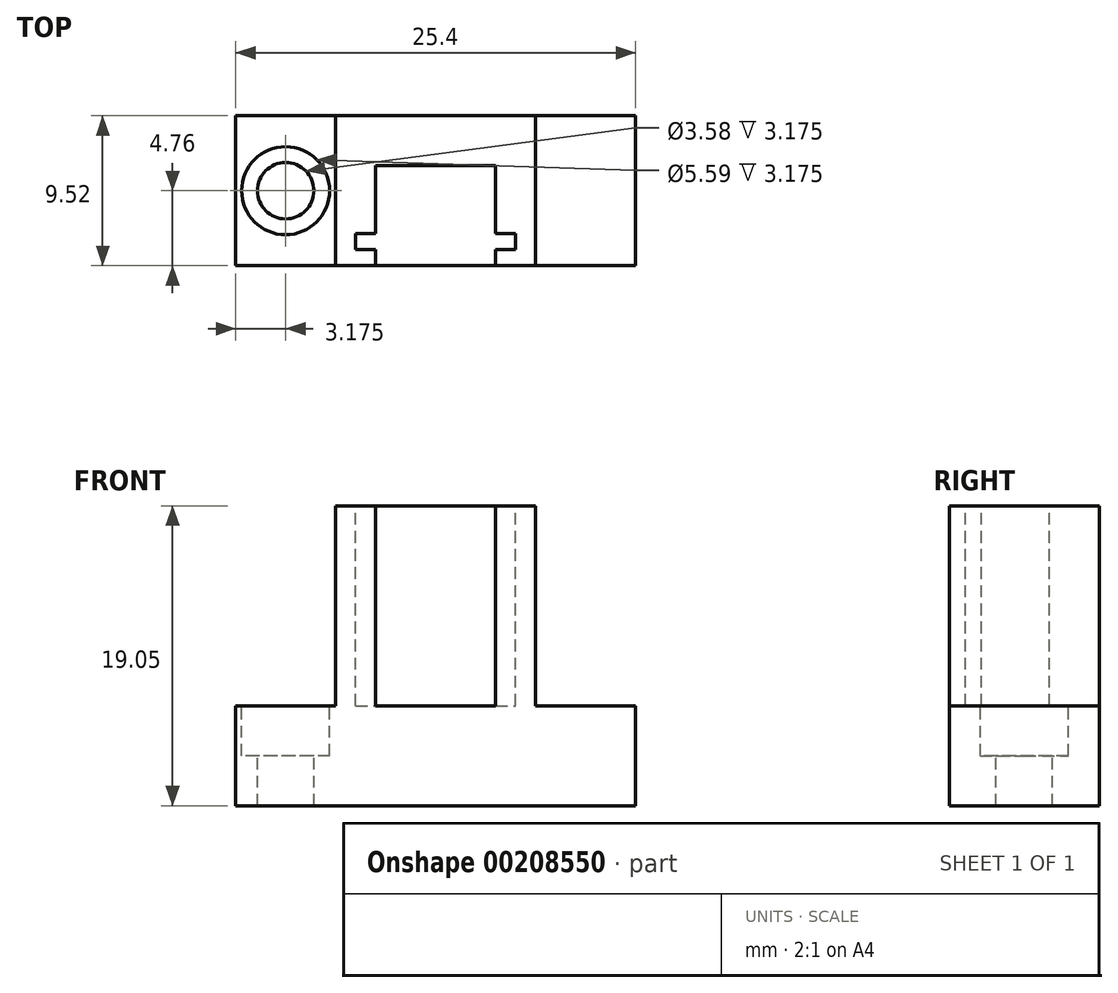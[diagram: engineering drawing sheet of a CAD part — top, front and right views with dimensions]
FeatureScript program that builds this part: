
annotation { "Feature Type Name" : "Feature", "Feature Type Description" : "" }
export const myFeature = defineFeature(function(context is Context, id is Id, definition is map)
    precondition{}
    {
        {
            var Q0;
            Q0=qCreatedBy(makeId("Top.planeOp"),FACE);
            var sketch = newSketch(context, id + "F0", { "sketchPlane" : qUnion([Q0])});
            skLineSegment(sketch, "E0.bottom", {"start": v(12.7, 4.76) * mm, "end": v(-12.7, 4.76) * mm});
            skLineSegment(sketch, "E0.top", {"start": v(12.7, -4.76) * mm, "end": v(-12.7, -4.76) * mm});
            skLineSegment(sketch, "E0.left", {"start": v(12.7, 4.76) * mm, "end": v(12.7, -4.76) * mm});
            skLineSegment(sketch, "E0.right", {"start": v(-12.7, 4.76) * mm, "end": v(-12.7, -4.76) * mm});
            skPoint(sketch, "E0.middle", {"position": v(0, 0) * mm});
            skSolve(sketch);
        }
        {
            var Q0;
            Q0=makeQuery(id+"F0.imprint","IMPRINT",FACE,{"disambiguationData":[TD([[makeQuery(id+"F0.imprint","IMPRINT",EDGE,{"derivedFrom":sQuery(id+"F0.wireOp",EDGE,"E0.bottom")}),1.0]])]});
            extrude(context, id + "F1", {"entities" : qUnion([Q0]), "depth" : 19.05 * mm});
        }
        {
            var Q0;
            Q0=makeQuery(id+"F1.opExtrude","SWEPT_FACE",FACE,{"disambiguationData":[OSD([sQuery(id+"F0.wireOp",EDGE,"E0.top")])]});
            var sketch = newSketch(context, id + "F2", { "sketchPlane" : qUnion([Q0])});
            skLineSegment(sketch, "E1", {"start": v(-12.7, 6.35) * mm, "end": v(-6.35, 6.35) * mm});
            skLineSegment(sketch, "E2", {"start": v(-6.35, 6.35) * mm, "end": v(-6.35, 19.05) * mm});
            skLineSegment(sketch, "E3", {"start": v(-6.35, 19.05) * mm, "end": v(0, 19.05) * mm});
            skLineSegment(sketch, "E4", {"start": v(0, 19.05) * mm, "end": v(0, 0) * mm, "construction": true});
            skLineSegment(sketch, "E5.MirrorCS", {"start": v(6.35, 19.05) * mm, "end": v(0, 19.05) * mm});
            skLineSegment(sketch, "E6.MirrorCS", {"start": v(12.7, 6.35) * mm, "end": v(6.35, 6.35) * mm});
            skLineSegment(sketch, "E7.MirrorCS", {"start": v(6.35, 6.35) * mm, "end": v(6.35, 19.05) * mm});
            skSolve(sketch);
        }
        {
            var Q0;
            {var subQ0=sQuery(id+"F2.wireOp",EDGE,"E1");Q0=makeQuery(id+"F2.imprint","IMPRINT",FACE,{"disambiguationData":[TD([[makeQuery(id+"F2.imprint","IMPRINT",EDGE,{"derivedFrom":subQ0}),1.0]])]});}
            var Q1;
            {var subQ0=sQuery(id+"F2.wireOp",EDGE,"E6.MirrorCS");Q1=makeQuery(id+"F2.imprint","IMPRINT",FACE,{"disambiguationData":[TD([[makeQuery(id+"F2.imprint","IMPRINT",EDGE,{"derivedFrom":subQ0}),-1.0]])]});}
            extrude(context, id + "F3", {"entities" : qUnion([Q0, Q1]), "operationType" : NewBodyOperationType.REMOVE, "oppositeDirection" : true, "depth" : 25.4 * mm});
        }
        {
            var Q0;
            Q0=makeQuery(id+"F3.boolean.opBoolean","COPY",FACE,{"derivedFrom":makeQuery(id+"F3.opExtrude","SWEPT_FACE",FACE,{"disambiguationData":[OSD([sQuery(id+"F2.wireOp",EDGE,"E1")])]})});
            var sketch = newSketch(context, id + "F4", { "sketchPlane" : qUnion([Q0])});
            skPoint(sketch, "E8", {"position": v(-9.53, 0) * mm});
            skPoint(sketch, "E8.positionSnap0", {"position": v(-12.7, 0) * mm});
            skSolve(sketch);
        }
        {
            var Q0;
            Q0=sQuery(id+"F4.wireOp",VERTEX,"E8");
            var Q1;
            Q1=makeQuery(id+"F1.opExtrude","SWEPT_BODY",BODY,{"disambiguationData":[OSD([sQuery(id+"F0.wireOp",EDGE,"E0.bottom"),sQuery(id+"F0.wireOp",EDGE,"E0.top"),sQuery(id+"F0.wireOp",EDGE,"E0.left"),sQuery(id+"F0.wireOp",EDGE,"E0.right")])]});
            hole(context, id + "F5", {"style" : HoleStyle.C_BORE, "endStyle" : HoleEndStyle.BLIND, "holeDiameter" : 3.58 * mm, "cBoreDiameter" : 5.6 * mm, "cBoreDepth" : 3.17 * mm, "holeDepth" : 6.73 * mm, "locations" : qUnion([Q0]), "scope" : qUnion([Q1])});
        }
        {
            var Q0;
            Q0=makeQuery(id+"F1.opExtrude","SWEPT_FACE",FACE,{"disambiguationData":[OSD([sQuery(id+"F0.wireOp",EDGE,"E0.top")])]});
            var sketch = newSketch(context, id + "F6", { "sketchPlane" : qUnion([Q0])});
            skLineSegment(sketch, "E9.bottom", {"start": v(-3.81, 6.35) * mm, "end": v(3.81, 6.35) * mm});
            skLineSegment(sketch, "E9.top", {"start": v(-3.81, 19.05) * mm, "end": v(3.8, 19.05) * mm});
            skLineSegment(sketch, "E9.left", {"start": v(3.81, 6.35) * mm, "end": v(3.8, 19.05) * mm});
            skLineSegment(sketch, "E9.right", {"start": v(-3.81, 6.35) * mm, "end": v(-3.81, 19.05) * mm});
            skSolve(sketch);
        }
        {
            var Q0;
            Q0=makeQuery(id+"F6.imprint","IMPRINT",FACE,{"disambiguationData":[TD([[makeQuery(id+"F6.imprint","IMPRINT",EDGE,{"derivedFrom":sQuery(id+"F6.wireOp",EDGE,"E9.bottom")}),1.0]])]});
            extrude(context, id + "F7", {"entities" : qUnion([Q0]), "operationType" : NewBodyOperationType.REMOVE, "oppositeDirection" : true, "depth" : 6.35 * mm});
        }
        {
            var Q0;
            Q0=makeQuery(id+"F1.opExtrude","CAP_FACE",FACE,{"disambiguationData":[OSD([sQuery(id+"F0.wireOp",EDGE,"E0.bottom"),sQuery(id+"F0.wireOp",EDGE,"E0.top"),sQuery(id+"F0.wireOp",EDGE,"E0.left"),sQuery(id+"F0.wireOp",EDGE,"E0.right")])],"isStart":false});
            var sketch = newSketch(context, id + "F8", { "sketchPlane" : qUnion([Q0])});
            skLineSegment(sketch, "E10.bottom", {"start": v(-5.08, -2.73) * mm, "end": v(5.08, -2.73) * mm});
            skLineSegment(sketch, "E10.top", {"start": v(-5.08, -3.75) * mm, "end": v(5.08, -3.75) * mm});
            skLineSegment(sketch, "E10.left", {"start": v(-5.08, -2.73) * mm, "end": v(-5.08, -3.75) * mm});
            skLineSegment(sketch, "E10.right", {"start": v(5.08, -2.73) * mm, "end": v(5.08, -3.75) * mm});
            skPoint(sketch, "E10.middle", {"position": v(0, -3.24) * mm});
            skSolve(sketch);
        }
        {
            var Q0;
            {var subQ0=sQuery(id+"F8.wireOp",EDGE,"E10.left");Q0=makeQuery(id+"F8.imprint","IMPRINT",FACE,{"disambiguationData":[TD([[makeQuery(id+"F8.imprint","IMPRINT",EDGE,{"derivedFrom":subQ0}),1.0]])]});}
            var Q1;
            {var subQ0=sQuery(id+"F8.wireOp",EDGE,"E10.right");Q1=makeQuery(id+"F8.imprint","IMPRINT",FACE,{"disambiguationData":[TD([[makeQuery(id+"F8.imprint","IMPRINT",EDGE,{"derivedFrom":subQ0}),-1.0]])]});}
            extrude(context, id + "F9", {"entities" : qUnion([Q0, Q1]), "operationType" : NewBodyOperationType.REMOVE, "oppositeDirection" : true, "depth" : 12.7 * mm});
        }
    });
